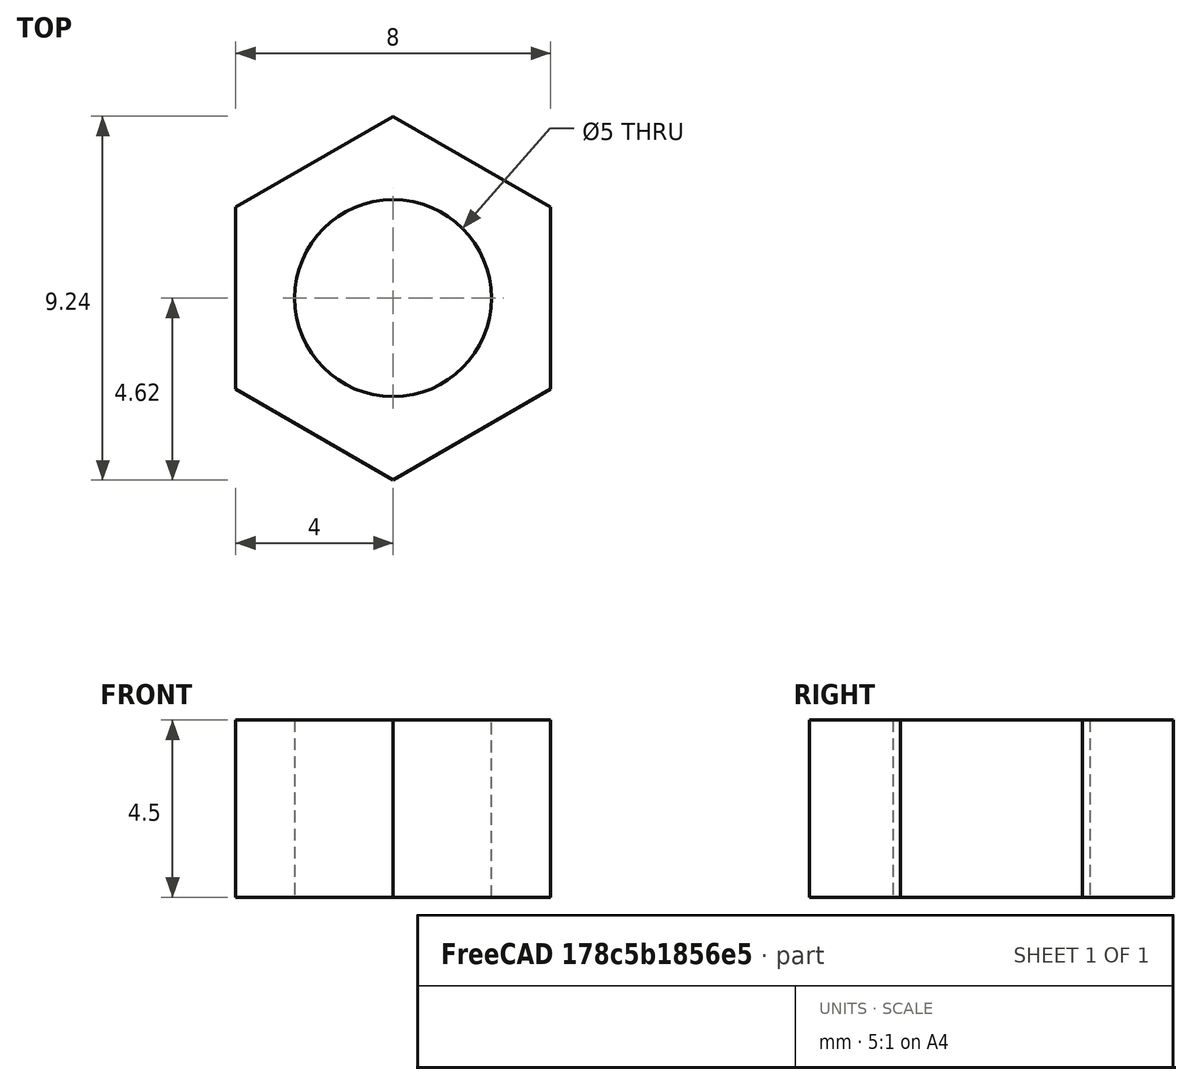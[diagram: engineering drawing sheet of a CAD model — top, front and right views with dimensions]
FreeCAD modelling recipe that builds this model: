
FCSTD DOCUMENT  (FreeCAD 0.18R14555 (Git shallow))
Label: m5-nut
License: All rights reserved
LicenseURL: http://en.wikipedia.org/wiki/All_rights_reserved
objects: Sketcher::SketchObject×1, PartDesign::Pad×1, PartDesign::Body×1
note: 4 computed .brp shape members not serialized (recipe doc carries the construction recipe); baked Part::Feature solids carry a one-line shape summary decoded from their .brp

FEATURE [Sketcher::SketchObject] Sketch
  MapMode = 5
  Support = -> [XY_Plane]
  sketch-geometry (8):
    g0: LineSegment StartX=4 StartY=2.3094 StartZ=0 EndX=0 EndY=4.6188 EndZ=0
    g1: LineSegment StartX=0 StartY=4.6188 StartZ=0 EndX=-4 EndY=2.3094 EndZ=0
    g2: LineSegment StartX=-4 StartY=2.3094 StartZ=0 EndX=-4 EndY=-2.3094 EndZ=0
    g3: LineSegment StartX=-4 StartY=-2.3094 StartZ=0 EndX=-9e-16 EndY=-4.6188 EndZ=0
    g4: LineSegment StartX=-9e-16 StartY=-4.6188 StartZ=0 EndX=4 EndY=-2.3094 EndZ=0
    g5: LineSegment StartX=4 StartY=-2.3094 StartZ=0 EndX=4 EndY=2.3094 EndZ=0
    g6: Circle [constr] CenterX=0 CenterY=0 CenterZ=0 NormalX=0 NormalY=0 NormalZ=1 AngleXU=0 Radius=4.6188
    g7: Circle CenterX=0 CenterY=0 CenterZ=0 NormalX=0 NormalY=0 NormalZ=1 AngleXU=0 Radius=2.5
  constraints (18):
    c: Coincident(g0,g1)
    c: Coincident(g1,g2)
    c: Coincident(g2,g3)
    c: Coincident(g3,g4)
    c: Coincident(g4,g5)
    c: Coincident(g5,g0)
    c: Equal(g0, g1-g5) x5
    c: PointOnObject(g0,g6)
    c: PointOnObject(g1,g6)
    c: PointOnObject(g2,g6)
    c: PointOnObject(g3,g6)
    c: PointOnObject(g4,g6)
    c: PointOnObject(g5,g6)
    c: Coincident(g6,g-1)
    c: Vertical(g5)
    c: DistanceX(g1,g0) = 8
    c: Coincident(g7,g-1)
    c: Radius(g7) = 2.5
FEATURE [PartDesign::Pad] Pad
  Length = 4.5
  Length2 = 100
  Profile = -> Sketch
  Type = 0
FEATURE [PartDesign::Body] Body
  Group = -> [Sketch,Pad]
  Origin = -> Origin
  Tip = -> Pad
